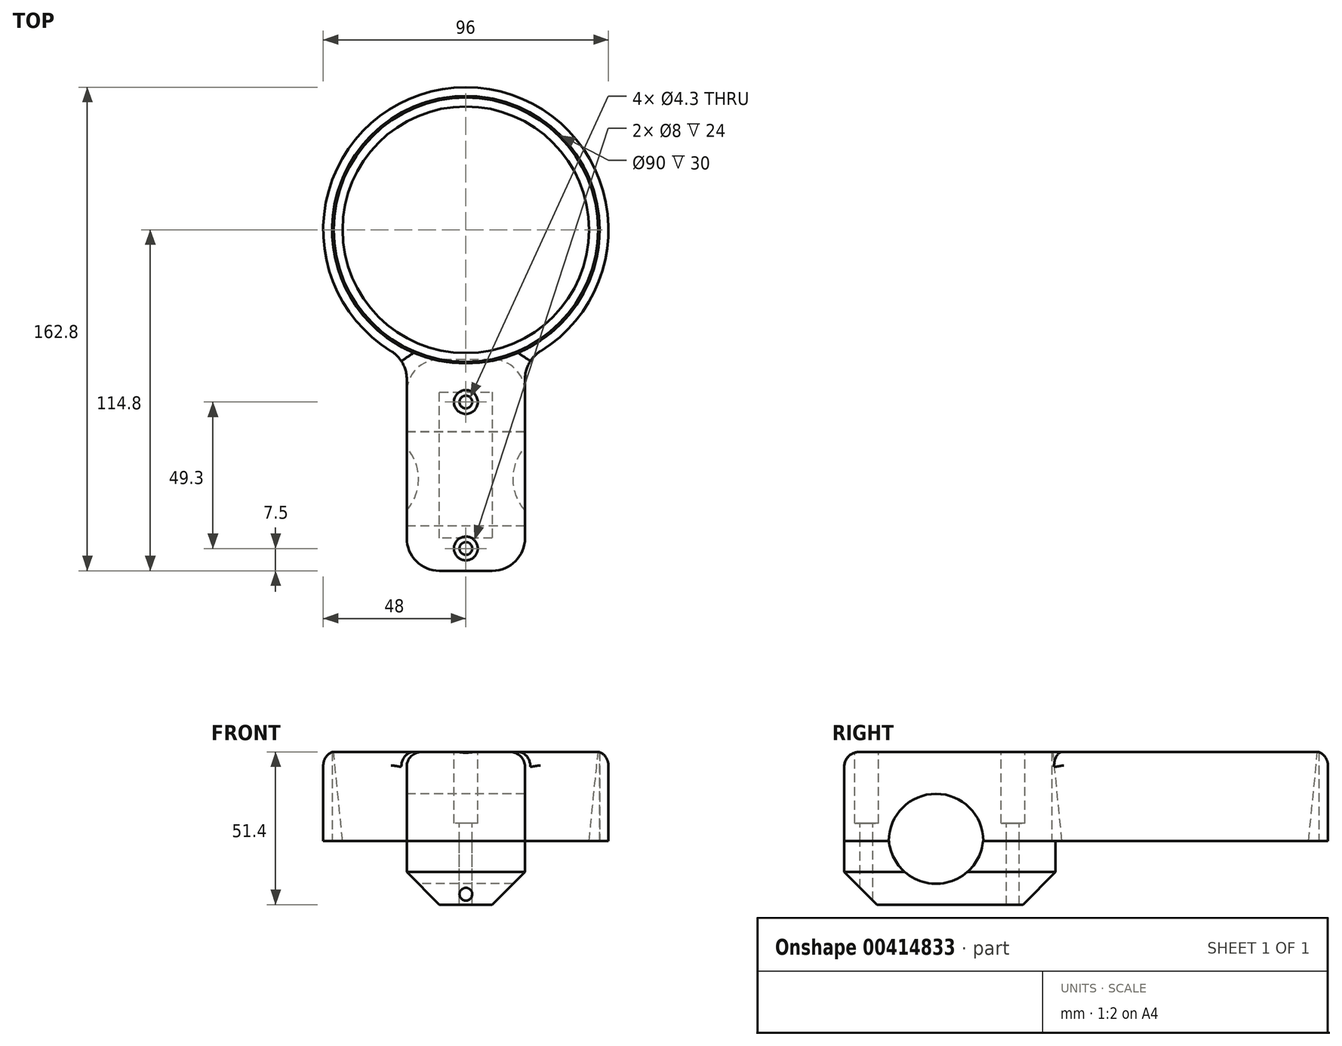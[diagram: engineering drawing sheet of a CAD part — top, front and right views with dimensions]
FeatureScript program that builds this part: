
annotation { "Feature Type Name" : "Feature", "Feature Type Description" : "" }
export const myFeature = defineFeature(function(context is Context, id is Id, definition is map)
    precondition{}
    {
        {
            var Q0;
            Q0=qCreatedBy(makeId("Right.planeOp"),FACE);
            var sketch = newSketch(context, id + "F0", { "sketchPlane" : qUnion([Q0])});
            skLineSegment(sketch, "E0", {"start": v(45, 0) * mm, "end": v(45, 30) * mm});
            skLineSegment(sketch, "E1", {"start": v(45, 30) * mm, "end": v(44.5, 30) * mm});
            skLineSegment(sketch, "E2", {"start": v(44.5, 30) * mm, "end": v(41.5, 0) * mm});
            skLineSegment(sketch, "E3", {"start": v(41.5, 0) * mm, "end": v(45, 0) * mm});
            skLineSegment(sketch, "E4", {"start": v(0, 0) * mm, "end": v(41.5, 0) * mm, "construction": true});
            skLineSegment(sketch, "E5", {"start": v(44.5, 30) * mm, "end": v(0, 30) * mm, "construction": true});
            skLineSegment(sketch, "E6", {"start": v(0, 30) * mm, "end": v(0, 0) * mm, "construction": true});
            skSolve(sketch);
        }
        {
            var Q0;
            Q0 = qSketchRegion(id + "F0", true);
            var Q1;
            Q1=sQuery(id+"F0.wireOp",EDGE,"E6");
            revolve(context, id + "F1", {"entities" : qUnion([Q0]), "axis" : qUnion([Q1]), "revolveType" : RevolveType.FULL});
        }
        {
            var Q0;
            Q0=qCreatedBy(makeId("Top.planeOp"),FACE);
            var sketch = newSketch(context, id + "F2", { "sketchPlane" : qUnion([Q0])});
            skCircle(sketch, "E7.0", {"center": v(0, 0) * mm, "radius": 45 * mm});
            skCircle(sketch, "E8.0", {"center": v(0, 0) * mm, "radius": 48 * mm});
            skLineSegment(sketch, "E9", {"start": v(-19.9, -43.68) * mm, "end": v(-19.9, -114.8) * mm});
            skLineSegment(sketch, "E10", {"start": v(-19.9, -114.8) * mm, "end": v(19.9, -114.8) * mm});
            skLineSegment(sketch, "E11", {"start": v(19.9, -114.8) * mm, "end": v(19.9, -43.68) * mm});
            skLineSegment(sketch, "E12", {"start": v(-19.9, -79.24) * mm, "end": v(0, -79.24) * mm, "construction": true});
            skLineSegment(sketch, "E13", {"start": v(0, -79.24) * mm, "end": v(19.9, -79.24) * mm, "construction": true});
            skLineSegment(sketch, "E14", {"start": v(0, -114.8) * mm, "end": v(0, -99.8) * mm, "construction": true});
            skLineSegment(sketch, "E15", {"start": v(0, -99.8) * mm, "end": v(0, -68) * mm, "construction": true});
            skLineSegment(sketch, "E16", {"start": v(0, -68) * mm, "end": v(0, -48) * mm, "construction": true});
            skSolve(sketch);
        }
        {
            var Q0;
            Q0=makeQuery(id+"F2.imprint","IMPRINT",FACE,{"disambiguationData":[TD([[makeQuery(id+"F2.imprint","IMPRINT",EDGE,{"derivedFrom":sQuery(id+"F2.wireOp",EDGE,"E7.0")}),-1.0]])]});
            var Q1;
            {var subQ0=sQuery(id+"F2.wireOp",EDGE,"E9");Q1=makeQuery(id+"F2.imprint","IMPRINT",FACE,{"disambiguationData":[TD([[makeQuery(id+"F2.imprint","IMPRINT",EDGE,{"derivedFrom":subQ0}),1.0]])]});}
            var Q2;
            Q2=makeQuery(id+"F1.opRevolve","SWEPT_FACE",FACE,{"disambiguationData":[OSD([sQuery(id+"F0.wireOp",EDGE,"E1")])]});
            extrude(context, id + "F3", {"entities" : qUnion([Q0, Q1]), "endBound" : BoundingType.UP_TO_SURFACE, "endBoundEntityFace" : qUnion([Q2]), "depth" : 25 * mm});
        }
        {
            var Q0;
            Q0=makeQuery(id+"F3.opExtrude","SWEPT_FACE",FACE,{"disambiguationData":[OSD([sQuery(id+"F2.wireOp",EDGE,"E9")])]});
            var sketch = newSketch(context, id + "F4", { "sketchPlane" : qUnion([Q0])});
            skCircle(sketch, "E17", {"center": v(83.9, 0) * mm, "radius": 15.9 * mm});
            skSolve(sketch);
        }
        {
            var Q0;
            Q0 = qSketchRegion(id + "F4", true);
            extrude(context, id + "F5", {"entities" : qUnion([Q0]), "operationType" : NewBodyOperationType.REMOVE, "endBound" : BoundingType.THROUGH_ALL, "oppositeDirection" : true, "depth" : 25 * mm});
        }
        {
            var Q0;
            Q0=makeQuery(id+"F3.opExtrude","SWEPT_FACE",FACE,{"disambiguationData":[OSD([sQuery(id+"F2.wireOp",EDGE,"E9")])]});
            var sketch = newSketch(context, id + "F6", { "sketchPlane" : qUnion([Q0])});
            skLineSegment(sketch, "E18.bottom", {"start": v(43.68, 0) * mm, "end": v(68.07, 0) * mm});
            skLineSegment(sketch, "E18.top", {"start": v(43.68, -21.4) * mm, "end": v(114.8, -21.4) * mm});
            skLineSegment(sketch, "E18.left", {"start": v(43.68, 0) * mm, "end": v(43.68, -21.4) * mm});
            skLineSegment(sketch, "E18.right", {"start": v(114.8, 0) * mm, "end": v(114.8, -21.4) * mm});
            skArc(sketch, "E19", {"start": v(68.07, 0) * mm, "mid": v(83.9, -14.4) * mm, "end": v(99.73, 0) * mm});
            skLineSegment(sketch, "E20", {"start": v(83.9, 1.5) * mm, "end": v(83.9, 0) * mm, "construction": true});
            skLineSegment(sketch, "E21", {"start": v(83.9, 0) * mm, "end": v(83.9, -14.4) * mm, "construction": true});
            skLineSegment(sketch, "E22", {"start": v(83.9, -14.4) * mm, "end": v(83.9, -21.4) * mm, "construction": true});
            skLineSegment(sketch, "E23.trimOffspring", {"start": v(99.73, 0) * mm, "end": v(114.8, 0) * mm});
            skSolve(sketch);
        }
        {
            var Q0;
            Q0 = qSketchRegion(id + "F6", true);
            var Q1;
            Q1=makeQuery(id+"F3.opExtrude","SWEPT_FACE",FACE,{"disambiguationData":[OSD([sQuery(id+"F2.wireOp",EDGE,"E11")])]});
            extrude(context, id + "F7", {"entities" : qUnion([Q0]), "endBound" : BoundingType.UP_TO_SURFACE, "oppositeDirection" : true, "endBoundEntityFace" : qUnion([Q1]), "depth" : 25 * mm});
        }
        {
            var Q0;
            Q0=makeQuery(id+"F3.opExtrude","CAP_FACE",FACE,{"disambiguationData":[OSD([sQuery(id+"F2.wireOp",EDGE,"E7.0"),sQuery(id+"F2.wireOp",EDGE,"E8.0"),sQuery(id+"F2.wireOp",EDGE,"E9"),sQuery(id+"F2.wireOp",EDGE,"E10"),sQuery(id+"F2.wireOp",EDGE,"E11")])],"isStart":false});
            var sketch = newSketch(context, id + "F8", { "sketchPlane" : qUnion([Q0])});
            skPoint(sketch, "E24", {"position": v(0, -58) * mm});
            skPoint(sketch, "E25", {"position": v(0, -107.3) * mm});
            skSolve(sketch);
        }
        {
            var Q0;
            Q0=sQuery(id+"F8.wireOp",VERTEX,"E24");
            var Q1;
            Q1=sQuery(id+"F8.wireOp",VERTEX,"E25");
            var Q2;
            Q2=makeQuery(id+"F3.opExtrude","SWEPT_BODY",BODY,{"disambiguationData":[OSD([sQuery(id+"F2.wireOp",EDGE,"E7.0"),sQuery(id+"F2.wireOp",EDGE,"E8.0"),sQuery(id+"F2.wireOp",EDGE,"E9"),sQuery(id+"F2.wireOp",EDGE,"E10"),sQuery(id+"F2.wireOp",EDGE,"E11")])]});
            var Q3;
            Q3=makeQuery(id+"F7.opExtrude","SWEPT_BODY",BODY,{"disambiguationData":[OSD([sQuery(id+"F6.wireOp",EDGE,"E18.bottom"),sQuery(id+"F6.wireOp",EDGE,"E18.top"),sQuery(id+"F6.wireOp",EDGE,"E18.left"),sQuery(id+"F6.wireOp",EDGE,"E18.right"),sQuery(id+"F6.wireOp",EDGE,"E19"),sQuery(id+"F6.wireOp",EDGE,"E23.trimOffspring")])]});
            hole(context, id + "F9", {"style" : HoleStyle.C_BORE, "endStyle" : HoleEndStyle.THROUGH, "holeDiameter" : 4.3 * mm, "cBoreDiameter" : 8 * mm, "cBoreDepth" : 24 * mm, "isTappedThrough" : true, "tappedDepth" : 12 * mm, "tapClearance" : 3, "locations" : qUnion([Q0, Q1]), "scope" : qUnion([Q2, Q3])});
        }
        {
            var Q0;
            Q0=makeQuery(id+"F3.opExtrude","SWEPT_EDGE",EDGE,{"disambiguationData":[OSD([sQuery(id+"F2.wireOp",EDGE,"E8.0"),sQuery(id+"F2.wireOp",EDGE,"E9")])]});
            var Q1;
            Q1=makeQuery(id+"F3.opExtrude","SWEPT_EDGE",EDGE,{"disambiguationData":[OSD([sQuery(id+"F2.wireOp",EDGE,"E8.0"),sQuery(id+"F2.wireOp",EDGE,"E11")])]});
            var Q2;
            Q2=makeQuery(id+"F3.opExtrude","SWEPT_EDGE",EDGE,{"disambiguationData":[OSD([sQuery(id+"F2.wireOp",EDGE,"E10"),sQuery(id+"F2.wireOp",EDGE,"E11")])]});
            var Q3;
            Q3=makeQuery(id+"F7.opExtrude","CAP_EDGE",EDGE,{"disambiguationData":[OSD([sQuery(id+"F6.wireOp",EDGE,"E18.right")])],"isStart":false});
            var Q4;
            Q4=makeQuery(id+"F3.opExtrude","SWEPT_EDGE",EDGE,{"disambiguationData":[OSD([sQuery(id+"F2.wireOp",EDGE,"E9"),sQuery(id+"F2.wireOp",EDGE,"E10")])]});
            var Q5;
            Q5=makeQuery(id+"F7.opExtrude","CAP_EDGE",EDGE,{"disambiguationData":[OSD([sQuery(id+"F6.wireOp",EDGE,"E18.right")])],"isStart":true});
            var Q6;
            Q6=makeQuery(id+"F7.opExtrude","CAP_EDGE",EDGE,{"disambiguationData":[OSD([sQuery(id+"F6.wireOp",EDGE,"E18.left")])],"isStart":true});
            var Q7;
            Q7=makeQuery(id+"F7.opExtrude","CAP_EDGE",EDGE,{"disambiguationData":[OSD([sQuery(id+"F6.wireOp",EDGE,"E18.left")])],"isStart":false});
            fillet(context, id + "F10", {"entities" : qUnion([Q0, Q1, Q2, Q3, Q4, Q5, Q6, Q7]), "radius" : 11 * mm, "tangentPropagation" : true, "allowEdgeOverflow" : false});
        }
        {
            var Q0;
            Q0=makeQuery(id+"F3.opExtrude","CAP_EDGE",EDGE,{"disambiguationData":[OSD([sQuery(id+"F2.wireOp",EDGE,"E9")])],"isStart":false});
            var Q1;
            {var subQ0=sQuery(id+"F2.wireOp",EDGE,"E10");var subQ1=sQuery(id+"F2.wireOp",EDGE,"E9");Q1=makeQuery(id+"F10.opFillet","BLEND_EDGE",EDGE,{"blendedFrom":[makeQuery(id+"F3.opExtrude","SWEPT_EDGE",EDGE,{"disambiguationData":[OSD([subQ1,subQ0])]}),makeQuery(id+"F3.opExtrude","CAP_FACE",FACE,{"disambiguationData":[OSD([sQuery(id+"F2.wireOp",EDGE,"E7.0"),sQuery(id+"F2.wireOp",EDGE,"E8.0"),subQ1,subQ0,sQuery(id+"F2.wireOp",EDGE,"E11")])],"isStart":false})],"blendedInto":[makeQuery(id+"F3.opExtrude","CAP_FACE",FACE,{"disambiguationData":[OSD([sQuery(id+"F2.wireOp",EDGE,"E7.0"),sQuery(id+"F2.wireOp",EDGE,"E8.0"),subQ1,subQ0,sQuery(id+"F2.wireOp",EDGE,"E11")])],"isStart":false})]});}
            var Q2;
            Q2=makeQuery(id+"F3.opExtrude","CAP_EDGE",EDGE,{"disambiguationData":[OSD([sQuery(id+"F2.wireOp",EDGE,"E10")])],"isStart":false});
            var Q3;
            {var subQ0=sQuery(id+"F2.wireOp",EDGE,"E11");var subQ1=sQuery(id+"F2.wireOp",EDGE,"E10");Q3=makeQuery(id+"F10.opFillet","BLEND_EDGE",EDGE,{"blendedFrom":[makeQuery(id+"F3.opExtrude","SWEPT_EDGE",EDGE,{"disambiguationData":[OSD([subQ1,subQ0])]}),makeQuery(id+"F3.opExtrude","CAP_FACE",FACE,{"disambiguationData":[OSD([sQuery(id+"F2.wireOp",EDGE,"E7.0"),sQuery(id+"F2.wireOp",EDGE,"E8.0"),sQuery(id+"F2.wireOp",EDGE,"E9"),subQ1,subQ0])],"isStart":false})],"blendedInto":[makeQuery(id+"F3.opExtrude","CAP_FACE",FACE,{"disambiguationData":[OSD([sQuery(id+"F2.wireOp",EDGE,"E7.0"),sQuery(id+"F2.wireOp",EDGE,"E8.0"),sQuery(id+"F2.wireOp",EDGE,"E9"),subQ1,subQ0])],"isStart":false})]});}
            var Q4;
            Q4=makeQuery(id+"F3.opExtrude","CAP_EDGE",EDGE,{"disambiguationData":[OSD([sQuery(id+"F2.wireOp",EDGE,"E11")])],"isStart":false});
            fillet(context, id + "F11", {"entities" : qUnion([Q0, Q1, Q2, Q3, Q4]), "radius" : 5 * mm, "tangentPropagation" : true, "allowEdgeOverflow" : false});
        }
        {
            var Q0;
            Q0=makeQuery(id+"F7.opExtrude","CAP_EDGE",EDGE,{"disambiguationData":[OSD([sQuery(id+"F6.wireOp",EDGE,"E18.top")])],"isStart":true});
            chamfer(context, id + "F12", {"entities" : qUnion([Q0]), "chamferType" : ChamferType.OFFSET_ANGLE, "width" : 11 * mm, "oppositeDirection" : false, "angle" : 45 * degree, "tangentPropagation" : true});
        }
    });
